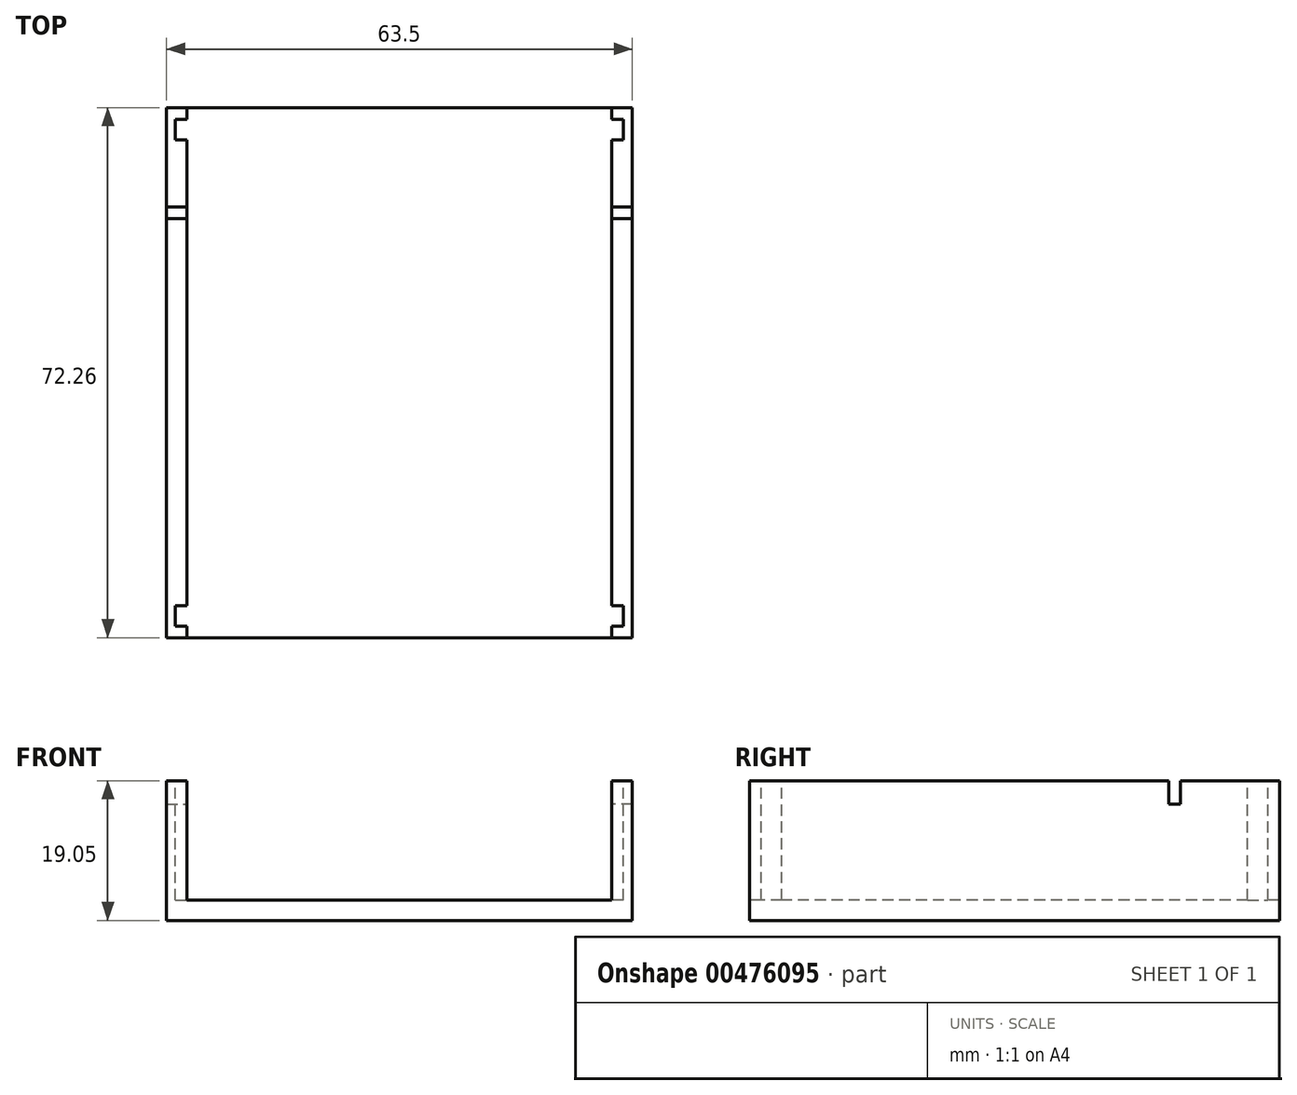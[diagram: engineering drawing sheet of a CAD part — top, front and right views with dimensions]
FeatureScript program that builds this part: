
annotation { "Feature Type Name" : "Feature", "Feature Type Description" : "" }
export const myFeature = defineFeature(function(context is Context, id is Id, definition is map)
    precondition{}
    {
        {
            var Q0;
            Q0=qCreatedBy(makeId("Top.planeOp"),FACE);
            var sketch = newSketch(context, id + "F0", { "sketchPlane" : qUnion([Q0])});
            skLineSegment(sketch, "E0.bottom", {"start": v(31.75, 36.13) * mm, "end": v(-31.75, 36.13) * mm});
            skLineSegment(sketch, "E0.top", {"start": v(31.75, -36.13) * mm, "end": v(-31.75, -36.13) * mm});
            skLineSegment(sketch, "E0.left", {"start": v(31.75, 36.13) * mm, "end": v(31.75, -36.13) * mm});
            skLineSegment(sketch, "E0.right", {"start": v(-31.75, 36.13) * mm, "end": v(-31.75, -36.13) * mm});
            skPoint(sketch, "E0.middle", {"position": v(0, 0) * mm});
            skSolve(sketch);
        }
        {
            var Q0;
            {var subQ0=sQuery(id+"F0.wireOp",EDGE,"4cc3bdc4-d607-4323-9014-4112534e357d.0");Q0=makeQuery(id+"F0.imprint","IMPRINT",FACE,{"disambiguationData":[TD([[makeQuery(id+"F0.imprint","IMPRINT",EDGE,{"derivedFrom":subQ0}),-1.0]])]});}
            var Q1;
            {var subQ0=sQuery(id+"F0.wireOp",EDGE,"E0.right");Q1=makeQuery(id+"F0.imprint","IMPRINT",FACE,{"disambiguationData":[TD([[makeQuery(id+"F0.imprint","IMPRINT",EDGE,{"derivedFrom":subQ0}),1.0]])]});}
            var Q2;
            {var subQ2=sQuery(id+"F0.wireOp",EDGE,"E0.left");Q2=makeQuery(id+"F0.imprint","IMPRINT",FACE,{"disambiguationData":[TD([[makeQuery(id+"F0.imprint","IMPRINT",EDGE,{"derivedFrom":subQ2}),-1.0]])]});}
            extrude(context, id + "F1", {"entities" : qUnion([Q0, Q1, Q2]), "oppositeDirection" : true, "depth" : 2.8 * mm, "offsetDistance" : 25.4 * mm});
        }
        {
            var Q0;
            Q0=makeQuery(id+"F1.opExtrude","CAP_FACE",FACE,{"disambiguationData":[OSD([sQuery(id+"F0.wireOp",EDGE,"E0.bottom"),sQuery(id+"F0.wireOp",EDGE,"E0.top"),sQuery(id+"F0.wireOp",EDGE,"E0.left"),sQuery(id+"F0.wireOp",EDGE,"E0.right")])],"isStart":true});
            var sketch = newSketch(context, id + "F2", { "sketchPlane" : qUnion([Q0])});
            skLineSegment(sketch, "E1", {"start": v(28.96, 36.13) * mm, "end": v(28.96, -36.13) * mm});
            skLineSegment(sketch, "E2", {"start": v(-28.96, 36.13) * mm, "end": v(-28.96, -36.13) * mm});
            skSolve(sketch);
        }
        {
            var Q0;
            Q0 = qSketchRegion(id + "F2", true);
            var Q1;
            {var subQ0=sQuery(id+"F2.wireOp",EDGE,"E2");Q1=makeQuery(id+"F2.imprint","IMPRINT",FACE,{"disambiguationData":[TD([[makeQuery(id+"F2.imprint","IMPRINT",EDGE,{"derivedFrom":subQ0}),-1.0]])]});}
            var Q2;
            {var subQ0=sQuery(id+"F2.wireOp",EDGE,"E1");Q2=makeQuery(id+"F2.imprint","IMPRINT",FACE,{"disambiguationData":[TD([[makeQuery(id+"F2.imprint","IMPRINT",EDGE,{"derivedFrom":subQ0}),1.0]])]});}
            extrude(context, id + "F3", {"entities" : qUnion([Q0, Q1, Q2]), "operationType" : NewBodyOperationType.ADD, "depth" : 16.26 * mm, "offsetDistance" : 25.4 * mm});
        }
        {
            var Q0;
            Q0=makeQuery(id+"F3.opExtrude","CAP_FACE",FACE,{"disambiguationData":[OSD([sQuery(id+"F0.wireOp",EDGE,"E0.bottom"),sQuery(id+"F0.wireOp",EDGE,"E0.top"),sQuery(id+"F0.wireOp",EDGE,"E0.right"),sQuery(id+"F2.wireOp",EDGE,"E2")])],"isStart":false});
            var sketch = newSketch(context, id + "F4", { "sketchPlane" : qUnion([Q0])});
            skLineSegment(sketch, "E3", {"start": v(-28.96, -34.54) * mm, "end": v(-30.54, -34.54) * mm});
            skLineSegment(sketch, "E4", {"start": v(-30.54, -34.54) * mm, "end": v(-30.54, -31.75) * mm});
            skLineSegment(sketch, "E5", {"start": v(-30.54, -31.75) * mm, "end": v(-28.96, -31.75) * mm});
            skLineSegment(sketch, "E6.MirrorCS", {"start": v(-30.54, 34.54) * mm, "end": v(-30.54, 31.75) * mm});
            skLineSegment(sketch, "E7.MirrorCS", {"start": v(-30.54, 31.75) * mm, "end": v(-28.96, 31.75) * mm});
            skLineSegment(sketch, "E8.MirrorCS", {"start": v(-28.96, 34.54) * mm, "end": v(-30.54, 34.54) * mm});
            skSolve(sketch);
        }
        {
            var Q0;
            Q0=makeQuery(id+"F4.imprint","IMPRINT",FACE,{"disambiguationData":[TD([[makeQuery(id+"F4.imprint","IMPRINT",EDGE,{"derivedFrom":sQuery(id+"F4.wireOp",EDGE,"E6.MirrorCS")}),1.0]])]});
            var Q1;
            {var subQ0=sQuery(id+"F4.wireOp",EDGE,"E3");Q1=makeQuery(id+"F4.imprint","IMPRINT",FACE,{"disambiguationData":[TD([[makeQuery(id+"F4.imprint","IMPRINT",EDGE,{"derivedFrom":subQ0}),-1.0]])]});}
            var Q2;
            Q2=makeQuery(id+"F1.opExtrude","CAP_FACE",FACE,{"disambiguationData":[OSD([sQuery(id+"F0.wireOp",EDGE,"E0.bottom"),sQuery(id+"F0.wireOp",EDGE,"E0.top"),sQuery(id+"F0.wireOp",EDGE,"E0.left"),sQuery(id+"F0.wireOp",EDGE,"E0.right")])],"isStart":true});
            extrude(context, id + "F5", {"entities" : qUnion([Q0, Q1]), "operationType" : NewBodyOperationType.REMOVE, "endBound" : BoundingType.UP_TO_SURFACE, "oppositeDirection" : true, "depth" : 25.4 * mm, "endBoundEntityFace" : qUnion([Q2]), "offsetDistance" : 25.4 * mm});
        }
        {
            var Q0;
            Q0=makeQuery(id+"F3.opExtrude","CAP_FACE",FACE,{"disambiguationData":[OSD([sQuery(id+"F0.wireOp",EDGE,"E0.bottom"),sQuery(id+"F0.wireOp",EDGE,"E0.top"),sQuery(id+"F0.wireOp",EDGE,"E0.left"),sQuery(id+"F2.wireOp",EDGE,"E1")])],"isStart":false});
            var sketch = newSketch(context, id + "F6", { "sketchPlane" : qUnion([Q0])});
            skLineSegment(sketch, "E9", {"start": v(28.96, 34.54) * mm, "end": v(30.54, 34.54) * mm});
            skLineSegment(sketch, "E10", {"start": v(30.54, 34.54) * mm, "end": v(30.54, 31.75) * mm});
            skLineSegment(sketch, "E11", {"start": v(30.54, 31.75) * mm, "end": v(28.96, 31.75) * mm});
            skLineSegment(sketch, "E12.MirrorCS", {"start": v(28.96, -34.54) * mm, "end": v(30.54, -34.54) * mm});
            skLineSegment(sketch, "E13.MirrorCS", {"start": v(30.54, -34.54) * mm, "end": v(30.54, -31.75) * mm});
            skLineSegment(sketch, "E14.MirrorCS", {"start": v(30.54, -31.75) * mm, "end": v(28.96, -31.75) * mm});
            skSolve(sketch);
        }
        {
            var Q0;
            Q0 = qSketchRegion(id + "F6", true);
            var Q1;
            {var subQ0=sQuery(id+"F6.wireOp",EDGE,"E9");Q1=makeQuery(id+"F6.imprint","IMPRINT",FACE,{"disambiguationData":[TD([[makeQuery(id+"F6.imprint","IMPRINT",EDGE,{"derivedFrom":subQ0}),-1.0]])]});}
            var Q2;
            {var subQ0=sQuery(id+"F6.wireOp",EDGE,"E12.MirrorCS");Q2=makeQuery(id+"F6.imprint","IMPRINT",FACE,{"disambiguationData":[TD([[makeQuery(id+"F6.imprint","IMPRINT",EDGE,{"derivedFrom":subQ0}),1.0]])]});}
            var Q3;
            Q3=makeQuery(id+"F1.opExtrude","CAP_FACE",FACE,{"disambiguationData":[OSD([sQuery(id+"F0.wireOp",EDGE,"E0.bottom"),sQuery(id+"F0.wireOp",EDGE,"E0.top"),sQuery(id+"F0.wireOp",EDGE,"E0.left"),sQuery(id+"F0.wireOp",EDGE,"E0.right")])],"isStart":true});
            extrude(context, id + "F7", {"entities" : qUnion([Q0, Q1, Q2]), "operationType" : NewBodyOperationType.REMOVE, "endBound" : BoundingType.UP_TO_SURFACE, "oppositeDirection" : true, "depth" : 25.4 * mm, "endBoundEntityFace" : qUnion([Q3]), "offsetDistance" : 25.4 * mm});
        }
        {
            var Q0;
            {var subQ0=sQuery(id+"F4.wireOp",EDGE,"E5");var subQ1=sQuery(id+"F2.wireOp",EDGE,"E2");Q0=makeQuery(id+"F5.boolean.opBoolean","SPLIT",FACE,{"disambiguationData":[TD([makeQuery(id+"F5.opExtrude","SWEPT_FACE",FACE,{"disambiguationData":[OSD([subQ0])]})])],"derivedFrom":makeQuery(id+"F3.opExtrude","SWEPT_FACE",FACE,{"disambiguationData":[OSD([subQ1])]})});}
            var sketch = newSketch(context, id + "F8", { "sketchPlane" : qUnion([Q0])});
            skLineSegment(sketch, "E15.bottom", {"start": v(21.02, 16.26) * mm, "end": v(22.6, 16.26) * mm});
            skLineSegment(sketch, "E15.top", {"start": v(21.02, 13.08) * mm, "end": v(22.6, 13.08) * mm});
            skLineSegment(sketch, "E15.left", {"start": v(21.02, 16.26) * mm, "end": v(21.02, 13.08) * mm});
            skLineSegment(sketch, "E15.right", {"start": v(22.6, 16.26) * mm, "end": v(22.6, 13.08) * mm});
            skSolve(sketch);
        }
        {
            var Q0;
            Q0 = qSketchRegion(id + "F8", true);
            var Q1;
            {var subQ0=sQuery(id+"F8.wireOp",EDGE,"q2I5HytD-Oa0g-Luj7-6Tx5-YUH9ib5jZUs2");Q1=makeQuery(id+"F8.imprint","IMPRINT",FACE,{"disambiguationData":[TD([[makeQuery(id+"F8.imprint","IMPRINT",EDGE,{"derivedFrom":subQ0}),1.0]])]});}
            var Q2;
            {var subQ0=sQuery(id+"F0.wireOp",EDGE,"E0.right");Q2=makeQuery(id+"F3.boolean.opBoolean","MERGE",FACE,{"derivedFrom":[makeQuery(id+"F1.opExtrude","SWEPT_FACE",FACE,{"disambiguationData":[OSD([subQ0])]}),makeQuery(id+"F3.opExtrude","SWEPT_FACE",FACE,{"disambiguationData":[OSD([subQ0])]})]});}
            extrude(context, id + "F9", {"entities" : qUnion([Q0, Q1]), "operationType" : NewBodyOperationType.REMOVE, "endBound" : BoundingType.UP_TO_SURFACE, "oppositeDirection" : true, "depth" : 25.4 * mm, "endBoundEntityFace" : qUnion([Q2]), "offsetDistance" : 25.4 * mm});
        }
        {
            var Q0;
            {var subQ0=sQuery(id+"F6.wireOp",EDGE,"E11");var subQ1=sQuery(id+"F2.wireOp",EDGE,"E1");Q0=makeQuery(id+"F7.boolean.opBoolean","SPLIT",FACE,{"disambiguationData":[TD([makeQuery(id+"F7.opExtrude","SWEPT_FACE",FACE,{"disambiguationData":[OSD([subQ0])]})])],"derivedFrom":makeQuery(id+"F3.opExtrude","SWEPT_FACE",FACE,{"disambiguationData":[OSD([subQ1])]})});}
            var sketch = newSketch(context, id + "F10", { "sketchPlane" : qUnion([Q0])});
            skLineSegment(sketch, "E16", {"start": v(-26.99, 16.26) * mm, "end": v(-24.8, 14.05) * mm});
            skLineSegment(sketch, "E17", {"start": v(-24.8, 14.05) * mm, "end": v(-22.59, 16.26) * mm});
            skLineSegment(sketch, "E18", {"start": v(-22.59, 16.26) * mm, "end": v(-21, 16.26) * mm});
            skLineSegment(sketch, "E19", {"start": v(-22.59, 16.26) * mm, "end": v(-22.59, 13.08) * mm});
            skLineSegment(sketch, "E20", {"start": v(-22.59, 13.08) * mm, "end": v(-21, 13.08) * mm});
            skLineSegment(sketch, "E21", {"start": v(-21, 16.26) * mm, "end": v(-21, 13.08) * mm});
            skSolve(sketch);
        }
        {
            var Q0;
            Q0=makeQuery(id+"F10.imprint","IMPRINT",FACE,{"disambiguationData":[TD([[makeQuery(id+"F10.imprint","IMPRINT",EDGE,{"derivedFrom":sQuery(id+"F10.wireOp",EDGE,"E18")}),-1.0]])]});
            var Q1;
            {var subQ0=sQuery(id+"F0.wireOp",EDGE,"E0.left");Q1=makeQuery(id+"F3.boolean.opBoolean","MERGE",FACE,{"derivedFrom":[makeQuery(id+"F1.opExtrude","SWEPT_FACE",FACE,{"disambiguationData":[OSD([subQ0])]}),makeQuery(id+"F3.opExtrude","SWEPT_FACE",FACE,{"disambiguationData":[OSD([subQ0])]})]});}
            extrude(context, id + "F11", {"entities" : qUnion([Q0]), "operationType" : NewBodyOperationType.REMOVE, "endBound" : BoundingType.UP_TO_SURFACE, "oppositeDirection" : true, "depth" : 25.4 * mm, "endBoundEntityFace" : qUnion([Q1]), "offsetDistance" : 25.4 * mm});
        }
    });
